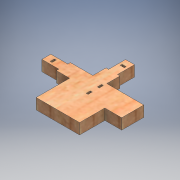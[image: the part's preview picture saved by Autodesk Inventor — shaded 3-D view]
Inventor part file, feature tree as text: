
AUTODESK INVENTOR PART (.ipt)
format: ipt  version: 2016 (Build 200138000, 138)  size: 195,072 bytes
history: native  units: mm
features: extrude x1, sketch x1
ambient origin geometry x8: Origin, YZ Plane, XZ Plane, XY Plane, X Axis, Y Axis, Z Axis, Center Point
bodies: Body1 (feature_tree)
feature tree (2):
  extrude  "Extrusion2"  Depth=10.1mm
  sketch  "Sketch1"  dims[d4=1.5mm d26=10.1mm d27=5.294635mm d31=2.5mm d32=1.1mm d35=5.5mm d41=1.1mm d42=2.5mm d72=17.5mm d89=6.39mm d90=0.0mm d99=5.5mm d103=12.0mm d104=10.0mm d105=13.147317mm d106=2.0mm d108=15.0mm d124=12.0mm]
